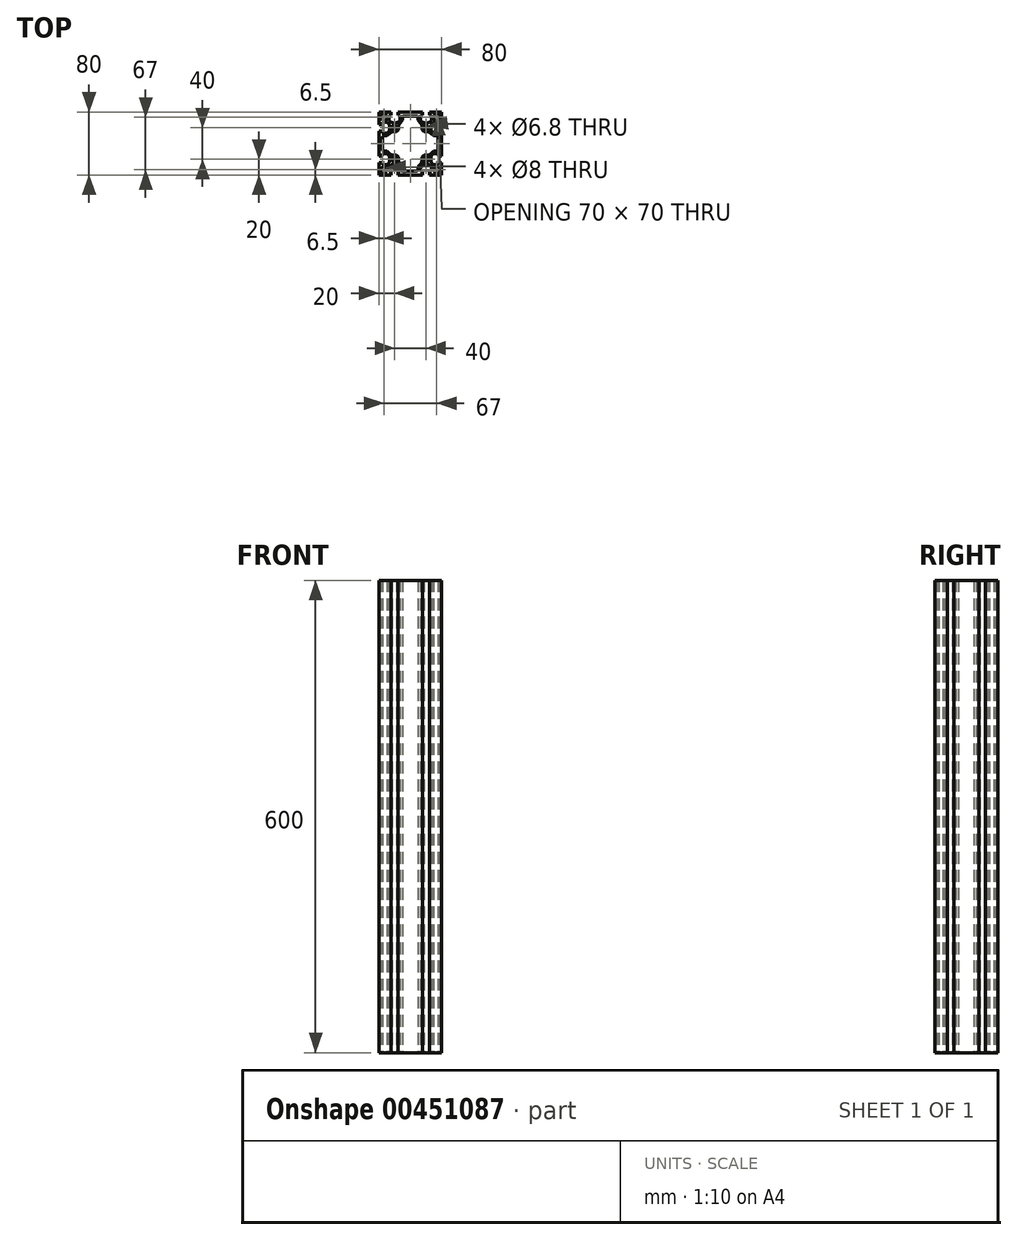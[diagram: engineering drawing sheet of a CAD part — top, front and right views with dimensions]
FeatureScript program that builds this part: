
annotation { "Feature Type Name" : "Feature", "Feature Type Description" : "" }
export const myFeature = defineFeature(function(context is Context, id is Id, definition is map)
    precondition{}
    {
        {
            var Q0;
            Q0=qCreatedBy(makeId("Top.planeOp"),FACE);
            var sketch = newSketch(context, id + "F0", { "sketchPlane" : qUnion([Q0])});
            skLineSegment(sketch, "E0.bottom", {"start": v(40, -40) * mm, "end": v(-40, -40) * mm});
            skLineSegment(sketch, "E0.top", {"start": v(40, 40) * mm, "end": v(-40, 40) * mm});
            skLineSegment(sketch, "E0.left", {"start": v(40, -40) * mm, "end": v(40, 40) * mm});
            skLineSegment(sketch, "E0.right", {"start": v(-40, -40) * mm, "end": v(-40, 40) * mm});
            skPoint(sketch, "E0.middle", {"position": v(0, 0) * mm});
            skLineSegment(sketch, "E1.top", {"start": v(-15.85, 40) * mm, "end": v(-24.15, 40) * mm});
            skLineSegment(sketch, "E1.left", {"start": v(-15.85, 36) * mm, "end": v(-15.85, 40) * mm});
            skLineSegment(sketch, "E1.right", {"start": v(-24.15, 36) * mm, "end": v(-24.15, 40) * mm});
            skPoint(sketch, "E1.middle", {"position": v(-20, 38) * mm});
            skLineSegment(sketch, "E2.bottom", {"start": v(-12.85, 36) * mm, "end": v(-15.85, 36) * mm});
            skLineSegment(sketch, "E2.left", {"start": v(-12.85, 36) * mm, "end": v(-12.85, 29.24) * mm});
            skLineSegment(sketch, "E2.right", {"start": v(-27.15, 36) * mm, "end": v(-27.15, 29.24) * mm});
            skPoint(sketch, "E2.middle", {"position": v(-20, 32.62) * mm});
            skArc(sketch, "E3", {"start": v(-27.15, 29.24) * mm, "mid": v(-20, 26) * mm, "end": v(-12.85, 29.24) * mm});
            skPoint(sketch, "E4.MirrorP", {"position": v(20, 32.62) * mm});
            skPoint(sketch, "E5.MirrorP", {"position": v(20, 38) * mm});
            skLineSegment(sketch, "E6.MirrorCS", {"start": v(15.85, 36) * mm, "end": v(15.85, 40) * mm});
            skLineSegment(sketch, "E7.MirrorCS", {"start": v(24.15, 36) * mm, "end": v(24.15, 40) * mm});
            skLineSegment(sketch, "E8.MirrorCS", {"start": v(12.85, 36) * mm, "end": v(15.85, 36) * mm});
            skLineSegment(sketch, "E9.MirrorCS", {"start": v(12.85, 36) * mm, "end": v(12.85, 29.24) * mm});
            skArc(sketch, "E10.MirrorCS", {"start": v(27.15, 29.24) * mm, "mid": v(20, 26) * mm, "end": v(12.85, 29.24) * mm});
            skLineSegment(sketch, "E11.MirrorCS", {"start": v(27.15, 36) * mm, "end": v(27.15, 29.24) * mm});
            skLineSegment(sketch, "E12.MirrorCS", {"start": v(15.85, 40) * mm, "end": v(24.15, 40) * mm});
            skLineSegment(sketch, "E13.1.0", {"start": v(36, 27.15) * mm, "end": v(29.24, 27.15) * mm});
            skLineSegment(sketch, "E13.1.1", {"start": v(36, 12.85) * mm, "end": v(29.24, 12.85) * mm});
            skArc(sketch, "E13.1.2", {"start": v(29.24, 27.15) * mm, "mid": v(26, 20) * mm, "end": v(29.24, 12.85) * mm});
            skLineSegment(sketch, "E13.1.3", {"start": v(36, -12.85) * mm, "end": v(29.24, -12.85) * mm});
            skLineSegment(sketch, "E13.1.4", {"start": v(36, -27.15) * mm, "end": v(29.24, -27.15) * mm});
            skPoint(sketch, "E13.1.5", {"position": v(38, 20) * mm});
            skPoint(sketch, "E13.1.6", {"position": v(38, -20) * mm});
            skArc(sketch, "E13.1.7", {"start": v(29.24, -27.15) * mm, "mid": v(26, -20) * mm, "end": v(29.24, -12.85) * mm});
            skPoint(sketch, "E13.1.8", {"position": v(32.62, -20) * mm});
            skPoint(sketch, "E13.1.9", {"position": v(32.62, 20) * mm});
            skLineSegment(sketch, "E13.1.10", {"start": v(36, 12.85) * mm, "end": v(36, 27.15) * mm});
            skLineSegment(sketch, "E13.1.11", {"start": v(36, -15.85) * mm, "end": v(36, -24.15) * mm});
            skLineSegment(sketch, "E13.1.12", {"start": v(40, 15.85) * mm, "end": v(40, 24.15) * mm});
            skLineSegment(sketch, "E13.1.13", {"start": v(40, -15.85) * mm, "end": v(40, -24.15) * mm});
            skLineSegment(sketch, "E13.1.14", {"start": v(36, 24.15) * mm, "end": v(40, 24.15) * mm});
            skLineSegment(sketch, "E13.1.15", {"start": v(36, 15.85) * mm, "end": v(40, 15.85) * mm});
            skLineSegment(sketch, "E13.1.16", {"start": v(36, 15.85) * mm, "end": v(36, 24.15) * mm});
            skLineSegment(sketch, "E13.1.17", {"start": v(36, -12.85) * mm, "end": v(36, -27.15) * mm});
            skLineSegment(sketch, "E13.1.18", {"start": v(36, -24.15) * mm, "end": v(40, -24.15) * mm});
            skLineSegment(sketch, "E13.1.19", {"start": v(36, -15.85) * mm, "end": v(40, -15.85) * mm});
            skLineSegment(sketch, "E13.2.0", {"start": v(27.15, -36) * mm, "end": v(27.15, -29.24) * mm});
            skLineSegment(sketch, "E13.2.1", {"start": v(12.85, -36) * mm, "end": v(12.85, -29.24) * mm});
            skArc(sketch, "E13.2.2", {"start": v(27.15, -29.24) * mm, "mid": v(20, -26) * mm, "end": v(12.85, -29.24) * mm});
            skLineSegment(sketch, "E13.2.3", {"start": v(-12.85, -36) * mm, "end": v(-12.85, -29.24) * mm});
            skLineSegment(sketch, "E13.2.4", {"start": v(-27.15, -36) * mm, "end": v(-27.15, -29.24) * mm});
            skPoint(sketch, "E13.2.5", {"position": v(20, -38) * mm});
            skPoint(sketch, "E13.2.6", {"position": v(-20, -38) * mm});
            skArc(sketch, "E13.2.7", {"start": v(-27.15, -29.24) * mm, "mid": v(-20, -26) * mm, "end": v(-12.85, -29.24) * mm});
            skPoint(sketch, "E13.2.8", {"position": v(-20, -32.62) * mm});
            skPoint(sketch, "E13.2.9", {"position": v(20, -32.62) * mm});
            skLineSegment(sketch, "E13.2.10", {"start": v(12.85, -36) * mm, "end": v(27.15, -36) * mm});
            skLineSegment(sketch, "E13.2.11", {"start": v(-15.85, -36) * mm, "end": v(-24.15, -36) * mm});
            skLineSegment(sketch, "E13.2.12", {"start": v(15.85, -40) * mm, "end": v(24.15, -40) * mm});
            skLineSegment(sketch, "E13.2.13", {"start": v(-15.85, -40) * mm, "end": v(-24.15, -40) * mm});
            skLineSegment(sketch, "E13.2.14", {"start": v(24.15, -36) * mm, "end": v(24.15, -40) * mm});
            skLineSegment(sketch, "E13.2.15", {"start": v(15.85, -36) * mm, "end": v(15.85, -40) * mm});
            skLineSegment(sketch, "E13.2.16", {"start": v(15.85, -36) * mm, "end": v(24.15, -36) * mm});
            skLineSegment(sketch, "E13.2.17", {"start": v(-12.85, -36) * mm, "end": v(-27.15, -36) * mm});
            skLineSegment(sketch, "E13.2.18", {"start": v(-24.15, -36) * mm, "end": v(-24.15, -40) * mm});
            skLineSegment(sketch, "E13.2.19", {"start": v(-15.85, -36) * mm, "end": v(-15.85, -40) * mm});
            skLineSegment(sketch, "E13.3.0", {"start": v(-36, -27.15) * mm, "end": v(-29.24, -27.15) * mm});
            skLineSegment(sketch, "E13.3.1", {"start": v(-36, -12.85) * mm, "end": v(-29.24, -12.85) * mm});
            skArc(sketch, "E13.3.2", {"start": v(-29.24, -27.15) * mm, "mid": v(-26, -20) * mm, "end": v(-29.24, -12.85) * mm});
            skLineSegment(sketch, "E13.3.3", {"start": v(-36, 12.85) * mm, "end": v(-29.24, 12.85) * mm});
            skLineSegment(sketch, "E13.3.4", {"start": v(-36, 27.15) * mm, "end": v(-29.24, 27.15) * mm});
            skPoint(sketch, "E13.3.5", {"position": v(-38, -20) * mm});
            skPoint(sketch, "E13.3.6", {"position": v(-38, 20) * mm});
            skArc(sketch, "E13.3.7", {"start": v(-29.24, 27.15) * mm, "mid": v(-26, 20) * mm, "end": v(-29.24, 12.85) * mm});
            skPoint(sketch, "E13.3.8", {"position": v(-32.62, 20) * mm});
            skPoint(sketch, "E13.3.9", {"position": v(-32.62, -20) * mm});
            skLineSegment(sketch, "E13.3.10", {"start": v(-36, -12.85) * mm, "end": v(-36, -27.15) * mm});
            skLineSegment(sketch, "E13.3.11", {"start": v(-36, 15.85) * mm, "end": v(-36, 24.15) * mm});
            skLineSegment(sketch, "E13.3.12", {"start": v(-40, -15.85) * mm, "end": v(-40, -24.15) * mm});
            skLineSegment(sketch, "E13.3.13", {"start": v(-40, 15.85) * mm, "end": v(-40, 24.15) * mm});
            skLineSegment(sketch, "E13.3.14", {"start": v(-36, -24.15) * mm, "end": v(-40, -24.15) * mm});
            skLineSegment(sketch, "E13.3.15", {"start": v(-36, -15.85) * mm, "end": v(-40, -15.85) * mm});
            skLineSegment(sketch, "E13.3.16", {"start": v(-36, -15.85) * mm, "end": v(-36, -24.15) * mm});
            skLineSegment(sketch, "E13.3.17", {"start": v(-36, 12.85) * mm, "end": v(-36, 27.15) * mm});
            skLineSegment(sketch, "E13.3.18", {"start": v(-36, 24.15) * mm, "end": v(-40, 24.15) * mm});
            skLineSegment(sketch, "E13.3.19", {"start": v(-36, 15.85) * mm, "end": v(-40, 15.85) * mm});
            skLineSegment(sketch, "E13.anchor1", {"start": v(0, 0) * mm, "end": v(-27.15, 29.24) * mm, "construction": true});
            skLineSegment(sketch, "E13.anchor2", {"start": v(0, 0) * mm, "end": v(-29.24, -27.15) * mm, "construction": true});
            skLineSegment(sketch, "E14.trimOffspring", {"start": v(-24.15, 36) * mm, "end": v(-27.15, 36) * mm});
            skLineSegment(sketch, "E15.trimOffspring", {"start": v(24.15, 36) * mm, "end": v(27.15, 36) * mm});
            skCircle(sketch, "E16", {"center": v(-20, 20) * mm, "radius": 3.4 * mm});
            skCircle(sketch, "E17", {"center": v(-33.5, 33.5) * mm, "radius": 4 * mm});
            skCircle(sketch, "E18.MirrorC", {"center": v(33.5, 33.5) * mm, "radius": 4 * mm});
            skCircle(sketch, "E19.MirrorC", {"center": v(33.5, -33.5) * mm, "radius": 4 * mm});
            skCircle(sketch, "E20.MirrorC", {"center": v(-33.5, -33.5) * mm, "radius": 4 * mm});
            skCircle(sketch, "E21.MirrorC", {"center": v(20, 20) * mm, "radius": 3.4 * mm});
            skCircle(sketch, "E22.MirrorC", {"center": v(20, -20) * mm, "radius": 3.4 * mm});
            skCircle(sketch, "E23.MirrorC", {"center": v(-20, -20) * mm, "radius": 3.4 * mm});
            skLineSegment(sketch, "E24", {"start": v(-10, 35) * mm, "end": v(0, 35) * mm});
            skLineSegment(sketch, "E25", {"start": v(-10, 35) * mm, "end": v(-10, 29.5) * mm});
            skLineSegment(sketch, "E26", {"start": v(-15, 17.5) * mm, "end": v(-15, 23.5) * mm});
            skLineSegment(sketch, "E27", {"start": v(-15, 23.5) * mm, "end": v(-10, 29.5) * mm});
            skLineSegment(sketch, "E28.MirrorCS", {"start": v(15, 17.5) * mm, "end": v(15, 23.5) * mm});
            skLineSegment(sketch, "E29.MirrorCS", {"start": v(15, 23.5) * mm, "end": v(10, 29.5) * mm});
            skLineSegment(sketch, "E30.MirrorCS", {"start": v(10, 35) * mm, "end": v(0, 35) * mm});
            skLineSegment(sketch, "E31.MirrorCS", {"start": v(10, 35) * mm, "end": v(10, 29.5) * mm});
            skLineSegment(sketch, "E32.1.0", {"start": v(-17.5, -15) * mm, "end": v(-23.5, -15) * mm});
            skLineSegment(sketch, "E32.1.1", {"start": v(-23.5, -15) * mm, "end": v(-29.5, -10) * mm});
            skLineSegment(sketch, "E32.1.2", {"start": v(-35, -10) * mm, "end": v(-29.5, -10) * mm});
            skLineSegment(sketch, "E32.1.3", {"start": v(-35, -10) * mm, "end": v(-35, 0) * mm});
            skLineSegment(sketch, "E32.1.4", {"start": v(-35, 10) * mm, "end": v(-35, 0) * mm});
            skLineSegment(sketch, "E32.1.5", {"start": v(-35, 10) * mm, "end": v(-29.5, 10) * mm});
            skLineSegment(sketch, "E32.1.6", {"start": v(-23.5, 15) * mm, "end": v(-29.5, 10) * mm});
            skLineSegment(sketch, "E32.1.7", {"start": v(-17.5, 15) * mm, "end": v(-23.5, 15) * mm});
            skLineSegment(sketch, "E32.2.0", {"start": v(15, -17.5) * mm, "end": v(15, -23.5) * mm});
            skLineSegment(sketch, "E32.2.1", {"start": v(15, -23.5) * mm, "end": v(10, -29.5) * mm});
            skLineSegment(sketch, "E32.2.2", {"start": v(10, -35) * mm, "end": v(10, -29.5) * mm});
            skLineSegment(sketch, "E32.2.3", {"start": v(10, -35) * mm, "end": v(0, -35) * mm});
            skLineSegment(sketch, "E32.2.4", {"start": v(-10, -35) * mm, "end": v(0, -35) * mm});
            skLineSegment(sketch, "E32.2.5", {"start": v(-10, -35) * mm, "end": v(-10, -29.5) * mm});
            skLineSegment(sketch, "E32.2.6", {"start": v(-15, -23.5) * mm, "end": v(-10, -29.5) * mm});
            skLineSegment(sketch, "E32.2.7", {"start": v(-15, -17.5) * mm, "end": v(-15, -23.5) * mm});
            skLineSegment(sketch, "E32.3.0", {"start": v(17.5, 15) * mm, "end": v(23.5, 15) * mm});
            skLineSegment(sketch, "E32.3.1", {"start": v(23.5, 15) * mm, "end": v(29.5, 10) * mm});
            skLineSegment(sketch, "E32.3.2", {"start": v(35, 10) * mm, "end": v(29.5, 10) * mm});
            skLineSegment(sketch, "E32.3.3", {"start": v(35, 10) * mm, "end": v(35, 0) * mm});
            skLineSegment(sketch, "E32.3.4", {"start": v(35, -10) * mm, "end": v(35, 0) * mm});
            skLineSegment(sketch, "E32.3.5", {"start": v(35, -10) * mm, "end": v(29.5, -10) * mm});
            skLineSegment(sketch, "E32.3.6", {"start": v(23.5, -15) * mm, "end": v(29.5, -10) * mm});
            skLineSegment(sketch, "E32.3.7", {"start": v(17.5, -15) * mm, "end": v(23.5, -15) * mm});
            skLineSegment(sketch, "E33", {"start": v(-15, 17.5) * mm, "end": v(-17.5, 15) * mm});
            skLineSegment(sketch, "E34", {"start": v(15, 17.5) * mm, "end": v(17.5, 15) * mm});
            skLineSegment(sketch, "E35", {"start": v(17.5, -15) * mm, "end": v(15, -17.5) * mm});
            skLineSegment(sketch, "E36", {"start": v(-15, -17.5) * mm, "end": v(-17.5, -15) * mm});
            skSolve(sketch);
        }
        {
            var Q0;
            {var subQ30=sQuery(id+"F0.wireOp",EDGE,"E1.left");Q0=makeQuery(id+"F0.imprint","IMPRINT",FACE,{"disambiguationData":[TD([[makeQuery(id+"F0.imprint","IMPRINT",EDGE,{"derivedFrom":subQ30}),-1.0]])]});}
            extrude(context, id + "F1", {"entities" : qUnion([Q0]), "depth" : 600 * mm});
        }
        {
            var Q0;
            Q0=makeQuery(id+"F1.opExtrude","SWEPT_EDGE",EDGE,{"disambiguationData":[OSD([sQuery(id+"F0.wireOp",EDGE,"E24"),sQuery(id+"F0.wireOp",EDGE,"E25")])]});
            var Q1;
            Q1=makeQuery(id+"F1.opExtrude","SWEPT_EDGE",EDGE,{"disambiguationData":[OSD([sQuery(id+"F0.wireOp",EDGE,"E30.MirrorCS"),sQuery(id+"F0.wireOp",EDGE,"E31.MirrorCS")])]});
            var Q2;
            Q2=makeQuery(id+"F1.opExtrude","SWEPT_EDGE",EDGE,{"disambiguationData":[OSD([sQuery(id+"F0.wireOp",EDGE,"E32.3.2"),sQuery(id+"F0.wireOp",EDGE,"E32.3.3")])]});
            var Q3;
            Q3=makeQuery(id+"F1.opExtrude","SWEPT_EDGE",EDGE,{"disambiguationData":[OSD([sQuery(id+"F0.wireOp",EDGE,"E32.3.4"),sQuery(id+"F0.wireOp",EDGE,"E32.3.5")])]});
            var Q4;
            Q4=makeQuery(id+"F1.opExtrude","SWEPT_EDGE",EDGE,{"disambiguationData":[OSD([sQuery(id+"F0.wireOp",EDGE,"E32.1.4"),sQuery(id+"F0.wireOp",EDGE,"E32.1.5")])]});
            var Q5;
            Q5=makeQuery(id+"F1.opExtrude","SWEPT_EDGE",EDGE,{"disambiguationData":[OSD([sQuery(id+"F0.wireOp",EDGE,"E32.1.2"),sQuery(id+"F0.wireOp",EDGE,"E32.1.3")])]});
            var Q6;
            Q6=makeQuery(id+"F1.opExtrude","SWEPT_EDGE",EDGE,{"disambiguationData":[OSD([sQuery(id+"F0.wireOp",EDGE,"E32.2.2"),sQuery(id+"F0.wireOp",EDGE,"E32.2.3")])]});
            var Q7;
            Q7=makeQuery(id+"F1.opExtrude","SWEPT_EDGE",EDGE,{"disambiguationData":[OSD([sQuery(id+"F0.wireOp",EDGE,"E32.2.4"),sQuery(id+"F0.wireOp",EDGE,"E32.2.5")])]});
            fillet(context, id + "F2", {"entities" : qUnion([Q0, Q1, Q2, Q3, Q4, Q5, Q6, Q7]), "radius" : 2 * mm, "tangentPropagation" : true, "allowEdgeOverflow" : false});
        }
        {
            var Q0;
            Q0=makeQuery(id+"F1.opExtrude","SWEPT_EDGE",EDGE,{"disambiguationData":[OSD([sQuery(id+"F0.wireOp",EDGE,"E26"),sQuery(id+"F0.wireOp",EDGE,"E27")])]});
            var Q1;
            Q1=makeQuery(id+"F1.opExtrude","SWEPT_EDGE",EDGE,{"disambiguationData":[OSD([sQuery(id+"F0.wireOp",EDGE,"E28.MirrorCS"),sQuery(id+"F0.wireOp",EDGE,"E29.MirrorCS")])]});
            var Q2;
            Q2=makeQuery(id+"F1.opExtrude","SWEPT_EDGE",EDGE,{"disambiguationData":[OSD([sQuery(id+"F0.wireOp",EDGE,"E32.3.0"),sQuery(id+"F0.wireOp",EDGE,"E32.3.1")])]});
            var Q3;
            Q3=makeQuery(id+"F1.opExtrude","SWEPT_EDGE",EDGE,{"disambiguationData":[OSD([sQuery(id+"F0.wireOp",EDGE,"E32.1.6"),sQuery(id+"F0.wireOp",EDGE,"E32.1.7")])]});
            var Q4;
            Q4=makeQuery(id+"F1.opExtrude","SWEPT_EDGE",EDGE,{"disambiguationData":[OSD([sQuery(id+"F0.wireOp",EDGE,"E32.1.0"),sQuery(id+"F0.wireOp",EDGE,"E32.1.1")])]});
            var Q5;
            Q5=makeQuery(id+"F1.opExtrude","SWEPT_EDGE",EDGE,{"disambiguationData":[OSD([sQuery(id+"F0.wireOp",EDGE,"E32.3.6"),sQuery(id+"F0.wireOp",EDGE,"E32.3.7")])]});
            var Q6;
            Q6=makeQuery(id+"F1.opExtrude","SWEPT_EDGE",EDGE,{"disambiguationData":[OSD([sQuery(id+"F0.wireOp",EDGE,"E32.2.0"),sQuery(id+"F0.wireOp",EDGE,"E32.2.1")])]});
            var Q7;
            Q7=makeQuery(id+"F1.opExtrude","SWEPT_EDGE",EDGE,{"disambiguationData":[OSD([sQuery(id+"F0.wireOp",EDGE,"E32.2.6"),sQuery(id+"F0.wireOp",EDGE,"E32.2.7")])]});
            fillet(context, id + "F3", {"entities" : qUnion([Q0, Q1, Q2, Q3, Q4, Q5, Q6, Q7]), "radius" : 7 * mm, "tangentPropagation" : true, "allowEdgeOverflow" : false});
        }
    });
